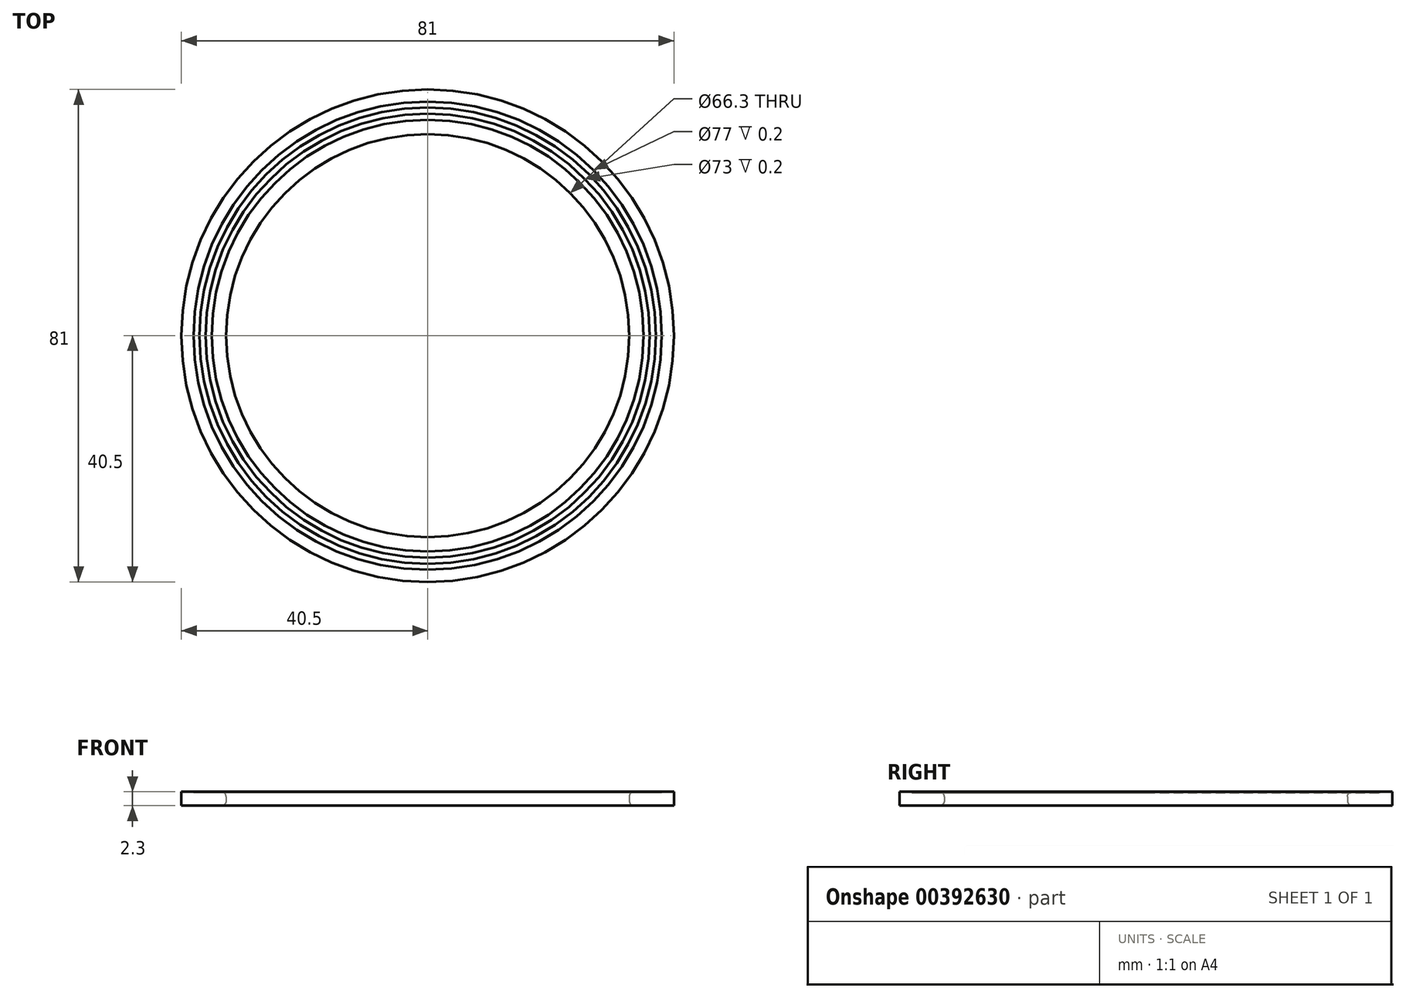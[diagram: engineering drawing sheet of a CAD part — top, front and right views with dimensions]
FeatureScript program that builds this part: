
annotation { "Feature Type Name" : "Feature", "Feature Type Description" : "" }
export const myFeature = defineFeature(function(context is Context, id is Id, definition is map)
    precondition{}
    {
        {
            var Q0;
            Q0=qCreatedBy(makeId("Top.planeOp"),FACE);
            var sketch = newSketch(context, id + "F0", { "sketchPlane" : qUnion([Q0])});
            skCircle(sketch, "E0", {"center": v(0, 0) * mm, "radius": 40.5 * mm});
            skCircle(sketch, "E1", {"center": v(0, 0) * mm, "radius": 33.15 * mm});
            skSolve(sketch);
        }
        {
            var Q0;
            Q0 = qSketchRegion(id + "F0", true);
            extrude(context, id + "F1", {"entities" : qUnion([Q0]), "depth" : 2.3 * mm});
        }
        {
            var Q0;
            Q0=makeQuery(id+"F1.opExtrude","CAP_EDGE",EDGE,{"disambiguationData":[OSD([sQuery(id+"F0.wireOp",EDGE,"E1")])],"isStart":false});
            var Q1;
            Q1=makeQuery(id+"F1.opExtrude","CAP_EDGE",EDGE,{"disambiguationData":[OSD([sQuery(id+"F0.wireOp",EDGE,"E1")])],"isStart":true});
            fillet(context, id + "F2", {"entities" : qUnion([Q0, Q1]), "radius" : 0.8 * mm, "tangentPropagation" : true, "allowEdgeOverflow" : false});
        }
        {
            var Q0;
            Q0=makeQuery(id+"F1.opExtrude","CAP_FACE",FACE,{"disambiguationData":[OSD([sQuery(id+"F0.wireOp",EDGE,"E0"),sQuery(id+"F0.wireOp",EDGE,"E1")])],"isStart":false});
            var sketch = newSketch(context, id + "F3", { "sketchPlane" : qUnion([Q0])});
            skCircle(sketch, "E2", {"center": v(0, 0) * mm, "radius": 38.5 * mm});
            skCircle(sketch, "E3", {"center": v(0, 0) * mm, "radius": 37.5 * mm});
            skCircle(sketch, "E4", {"center": v(0, 0) * mm, "radius": 36.5 * mm});
            skCircle(sketch, "E5", {"center": v(0, 0) * mm, "radius": 35.5 * mm});
            skSolve(sketch);
        }
        {
            var Q0;
            Q0 = qSketchRegion(id + "F3", true);
            var Q1;
            Q1=makeQuery(id+"F3.imprint","IMPRINT",FACE,{"disambiguationData":[TD([[makeQuery(id+"F3.imprint","IMPRINT",EDGE,{"derivedFrom":sQuery(id+"F3.wireOp",EDGE,"E4")}),1.0]])]});
            extrude(context, id + "F4", {"entities" : qUnion([Q0, Q1]), "operationType" : NewBodyOperationType.REMOVE, "oppositeDirection" : true, "depth" : 0.2 * mm});
        }
    });
